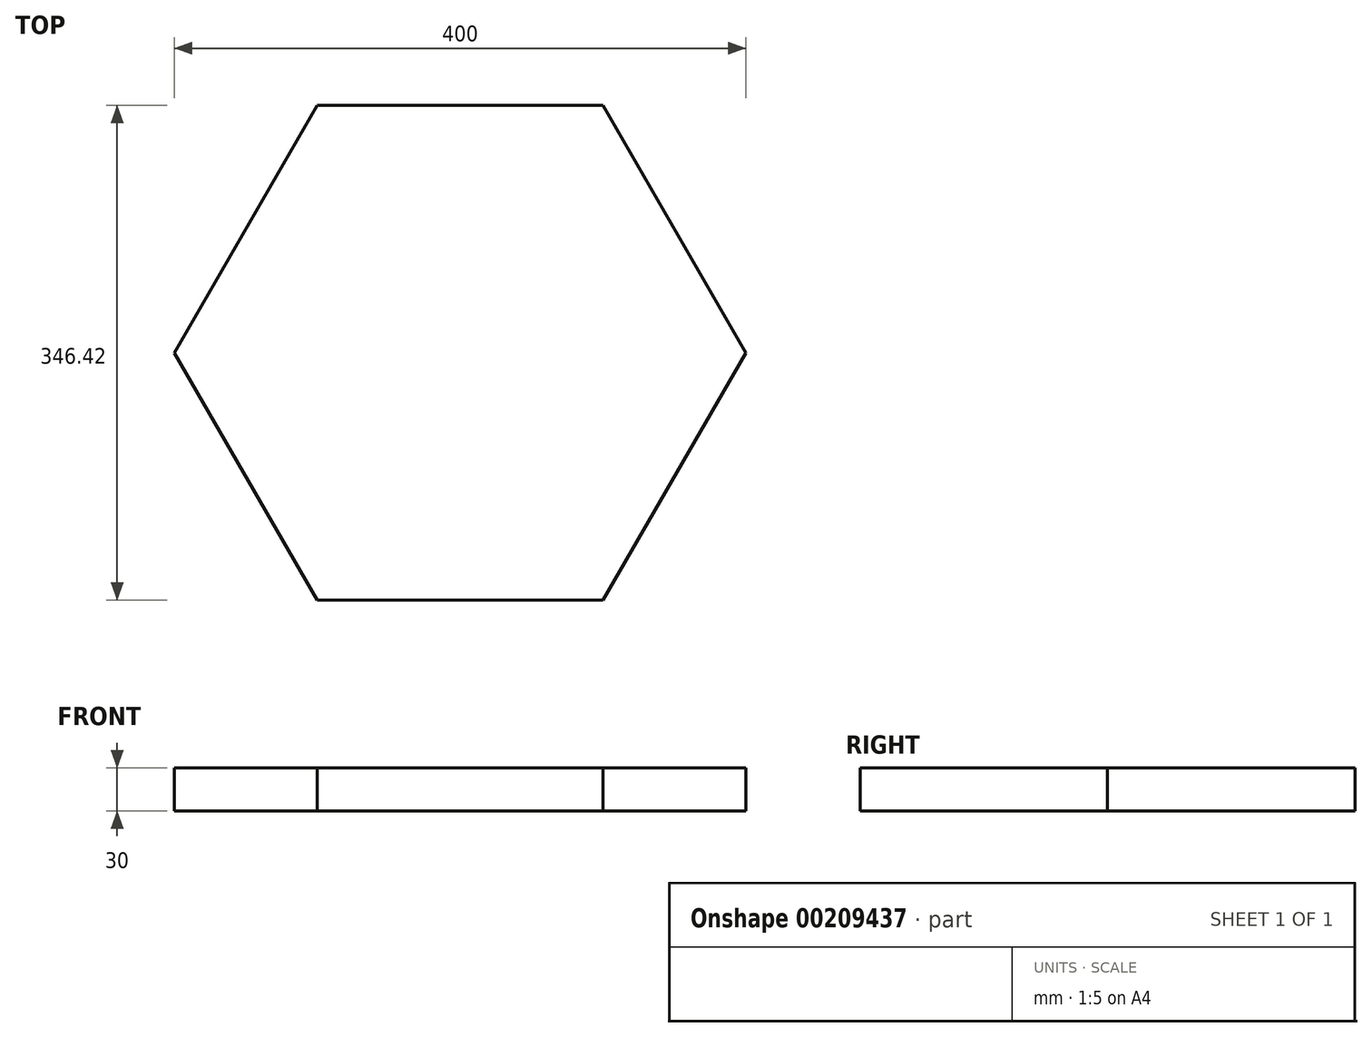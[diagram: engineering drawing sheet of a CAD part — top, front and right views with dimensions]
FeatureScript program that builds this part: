
annotation { "Feature Type Name" : "Feature", "Feature Type Description" : "" }
export const myFeature = defineFeature(function(context is Context, id is Id, definition is map)
    precondition{}
    {
        {
            var Q0;
            Q0=qCreatedBy(makeId("Top.planeOp"),FACE);
            var sketch = newSketch(context, id + "F0", { "sketchPlane" : qUnion([Q0])});
            skCircle(sketch, "E0.cCircle", {"center": v(-103.97, -69.15) * mm, "radius": 173.2 * mm, "construction": true});
            skLineSegment(sketch, "E0.0", {"start": v(-203.97, 104.06) * mm, "end": v(-3.97, 104.06) * mm});
            skLineSegment(sketch, "E0.1", {"start": v(-3.97, 104.06) * mm, "end": v(96.03, -69.15) * mm});
            skLineSegment(sketch, "E0.2", {"start": v(96.03, -69.15) * mm, "end": v(-3.97, -242.36) * mm});
            skLineSegment(sketch, "E0.3", {"start": v(-3.97, -242.36) * mm, "end": v(-203.97, -242.36) * mm});
            skLineSegment(sketch, "E0.4", {"start": v(-203.97, -242.36) * mm, "end": v(-303.97, -69.15) * mm});
            skLineSegment(sketch, "E0.5", {"start": v(-303.97, -69.15) * mm, "end": v(-203.97, 104.06) * mm});
            skPoint(sketch, "E0.0.midPoint", {"position": v(-103.97, 104.06) * mm});
            skSolve(sketch);
        }
        {
            var Q0;
            Q0=makeQuery(id+"F0.imprint","IMPRINT",FACE,{"disambiguationData":[TD([[makeQuery(id+"F0.imprint","IMPRINT",EDGE,{"derivedFrom":sQuery(id+"F0.wireOp",EDGE,"E0.0")}),-1.0]])]});
            extrude(context, id + "F1", {"entities" : qUnion([Q0]), "depth" : 30 * mm});
        }
    });
